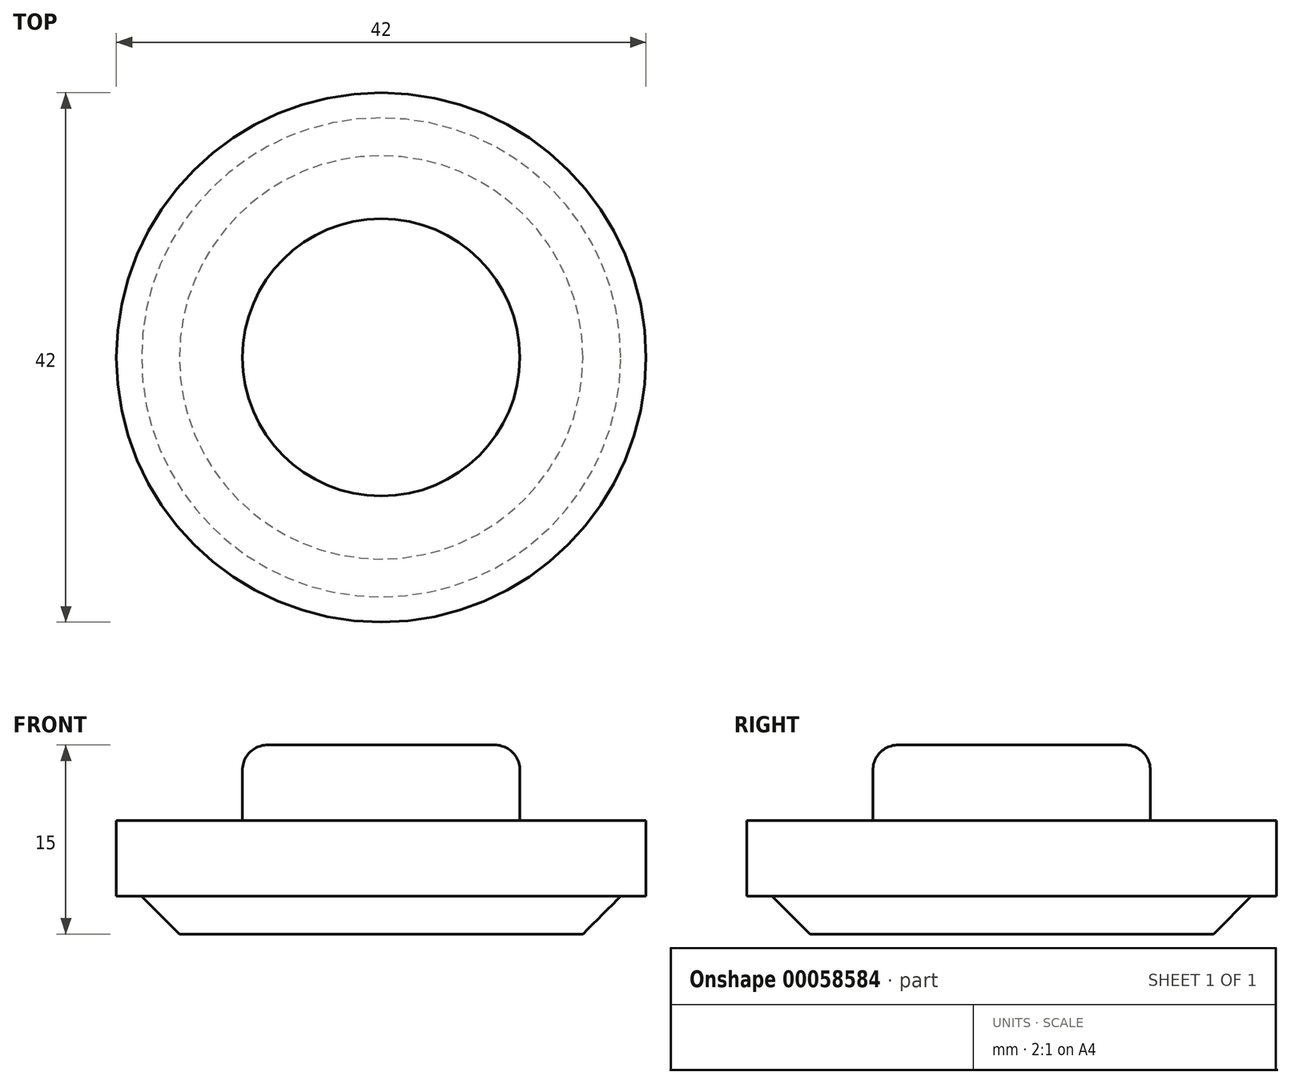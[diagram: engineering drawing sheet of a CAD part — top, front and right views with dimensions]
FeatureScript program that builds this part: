
annotation { "Feature Type Name" : "Feature", "Feature Type Description" : "" }
export const myFeature = defineFeature(function(context is Context, id is Id, definition is map)
    precondition{}
    {
        {
            var Q0;
            Q0=qCreatedBy(makeId("Front.planeOp"),FACE);
            var sketch = newSketch(context, id + "F0", { "sketchPlane" : qUnion([Q0])});
            skLineSegment(sketch, "E0", {"start": v(0, 15) * mm, "end": v(0, 0) * mm});
            skLineSegment(sketch, "E1", {"start": v(0, 0) * mm, "end": v(16, 0) * mm});
            skLineSegment(sketch, "E2", {"start": v(16, 0) * mm, "end": v(19, 3) * mm});
            skLineSegment(sketch, "E3", {"start": v(19, 3) * mm, "end": v(21, 3) * mm});
            skLineSegment(sketch, "E4", {"start": v(21, 3) * mm, "end": v(21, 9) * mm});
            skLineSegment(sketch, "E5", {"start": v(21, 9) * mm, "end": v(11, 9) * mm});
            skLineSegment(sketch, "E6", {"start": v(11, 9) * mm, "end": v(11, 13) * mm});
            skLineSegment(sketch, "E7", {"start": v(9, 15) * mm, "end": v(0, 15) * mm});
            skPoint(sketch, "E8.visualSharp", {"position": v(11, 15) * mm});
            skArc(sketch, "E8.filletArc", {"start": v(11, 13) * mm, "mid": v(10.41, 14.41) * mm, "end": v(9, 15) * mm});
            skSolve(sketch);
        }
        {
            var Q0;
            Q0 = qSketchRegion(id + "F0", true);
            var Q1;
            Q1=sQuery(id+"F0.wireOp",EDGE,"E0");
            revolve(context, id + "F1", {"entities" : qUnion([Q0]), "axis" : qUnion([Q1]), "revolveType" : RevolveType.FULL});
        }
    });
